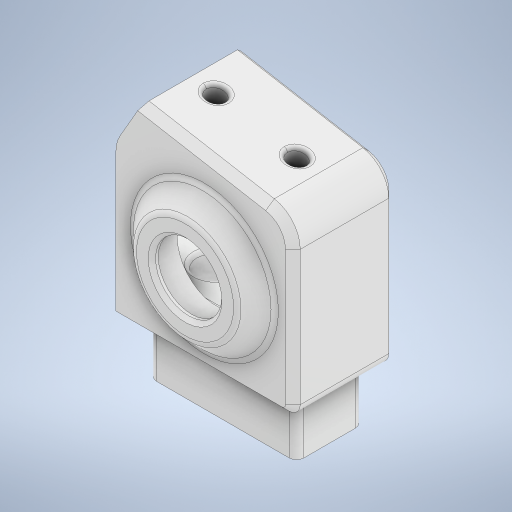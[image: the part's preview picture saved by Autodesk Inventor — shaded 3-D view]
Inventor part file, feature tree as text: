
AUTODESK INVENTOR PART (.ipt)
format: ipt  version: 2024 (Build 280153000, 153)  size: 552,448 bytes
history: native  units: mm
features: sketch x9, extrude x8, fillet x8, plane x6, projected_geometry x6, chamfer x3, hole x3
ambient origin geometry x8: Origin, YZ Plane, XZ Plane, XY Plane, X Axis, Y Axis, Z Axis, Center Point
bodies: Solid1 (feature_tree)
feature tree (43):
  extrude  "Extrusion1"  Depth=48.0mm
  extrude  "Extrusion2"  Depth=31.0mm
  sketch  "Sketch4"  dims[d4=19.198622mm d5=150.0deg d6=28.0mm d7=0.0mm d17=22.25mm]
  plane  "Work Plane1"
  plane  "Work Plane2"
  extrude  "Extrusion4"  TaperAngle=150.0deg  [1 undecoded]
  fillet  "Fillet1"  Radius=28.0mm
  fillet  "Fillet2"  Radius=22.25mm
  plane  "Work Plane6"
  plane  "Work Plane7"
  extrude  "Extrusion9"  [1 undecoded]
  plane  "Work Plane8"
  extrude  "Extrusion10"  Depth=16.0mm TaperAngle=0.0deg
  sketch  "Sketch14"  dims[d74=40.0mm d75=14.0mm d76=0.0mm d79=9.0mm d80=9.0mm d81=9.0mm d82=9.0mm d83=22.0mm d84=5.3mm d85=6.0mm d86=4.0mm d87=2.0mm d88=90.0deg d89=10.0mm d90=0.0mm d91=10.0mm d92=6.0mm d93=4.0mm d94=2.0mm d95=90.0deg d96=10.0mm d97=0.0mm d98=5.0mm d99=6.0mm d100=4.0mm d101=2.0mm d102=90.0deg d103=8.0mm d104=0.0mm d105=2.0mm d106=1.0mm d107=1.0mm d108=1.0mm d110=23.0mm d111=-9.0mm d112=-9.0mm d113=28.0mm d114=10.0mm d115=0.0mm d116=-7.25mm d117=18.0mm d118=10.0mm d119=0.0mm d120=5.25mm d121=2.0mm d122=45.0deg d123=10.0mm d124=0.0mm d125=-7.25mm d126=10.0mm d127=0.0mm d129=2.0mm d130=1.0mm d131=2.0mm d132=45.0deg d133=0.0mm]
  extrude  "Extrusion11"  Depth=1.0mm
  plane  "Work Plane9"
  extrude  "Extrusion12"  Depth=2.0mm TaperAngle=45.0deg
  chamfer  "Chamfer4"  Distance=14.0mm
  fillet  "Fillet8"  Radius=9.0mm
  chamfer  "Chamfer3"  Distance=9.0mm
  extrude  "Extrusion8"  Depth=9.0mm
  hole  "Hole4"  [1 undecoded]
  sketch  "Sketch11"  dims[d27=1.0mm d28=1.0mm]
  hole  "Hole5"  [1 undecoded]
  hole  "Hole6"  [1 undecoded]
  fillet  "Fillet11"  Radius=1.0mm
  fillet  "Fillet12"  Radius=1.0mm
  fillet  "Fillet13"  Radius=1.0mm
  fillet  "Fillet14"  Radius=23.0mm
  fillet  "Fillet16"  [1 undecoded]
  chamfer  "Chamfer5"  [1 undecoded]
  sketch  "Sketch1"  dims[d0=48.0mm d1=48.0mm]
  sketch  "Sketch3"  dims[d2=31.0mm d3=31.0mm]
  sketch  "Sketch9"  dims[d18=0.0mm d19=0.0mm d23=-3.75mm]
  sketch  "Sketch10"  dims[d24=-3.75mm d25=16.0mm d26=0.0mm]
  projected_geometry  "Projected Loop2"
  projected_geometry  "Projected Loop3"
  projected_geometry  "Projected Loop4"
  sketch  "Sketch12"  dims[d67=3.0mm d68=2.0mm d69=2.0mm d70=45.0deg]
  projected_geometry  "Projected Loop5"
  sketch  "Sketch13"  dims[d73=18.0mm]
  projected_geometry  "Projected Loop6"
  projected_geometry  "Project Cut Edges1"
note: 7 required parameter values undecoded (feature->parameter linkage not recoverable at this tier; creation-order binding heuristic only, values carry confidence <= 0.55)
